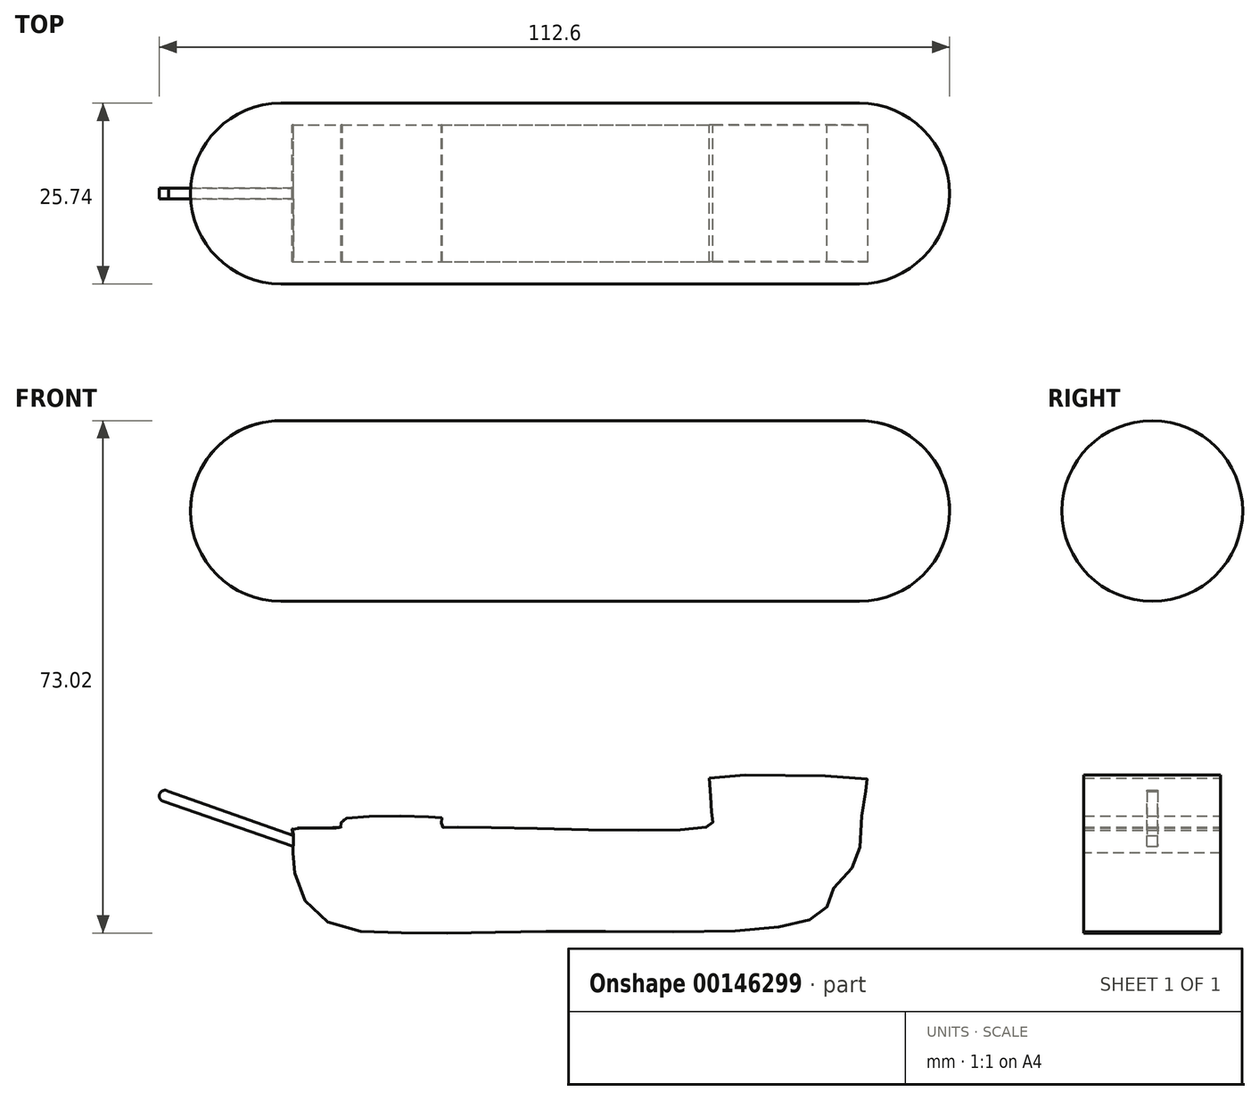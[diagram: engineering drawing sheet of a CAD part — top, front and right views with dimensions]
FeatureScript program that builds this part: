
annotation { "Feature Type Name" : "Feature", "Feature Type Description" : "" }
export const myFeature = defineFeature(function(context is Context, id is Id, definition is map)
    precondition{}
    {
        {
            var Q0;
            Q0=qCreatedBy(makeId("Front.planeOp"),FACE);
            var sketch = newSketch(context, id + "F0", { "sketchPlane" : qUnion([Q0])});
            skLineSegment(sketch, "E0.top", {"start": v(0, 25.75) * mm, "end": v(-41.2, 25.75) * mm});
            skLineSegment(sketch, "E0.left", {"start": v(0, 0) * mm, "end": v(0, 25.75) * mm});
            skLineSegment(sketch, "E0.right", {"start": v(-41.2, 12.87) * mm, "end": v(-41.2, 25.75) * mm});
            skArc(sketch, "E1", {"start": v(-41.2, 25.75) * mm, "mid": v(-50.3, 21.98) * mm, "end": v(-54.07, 12.87) * mm});
            skLineSegment(sketch, "E2.MirrorCS", {"start": v(0, 25.75) * mm, "end": v(41.2, 25.75) * mm});
            skLineSegment(sketch, "E3.MirrorCS", {"start": v(41.2, 12.87) * mm, "end": v(41.2, 25.75) * mm});
            skArc(sketch, "E4.MirrorCS", {"start": v(41.2, 25.75) * mm, "mid": v(50.3, 21.98) * mm, "end": v(54.07, 12.87) * mm});
            skPoint(sketch, "E5", {"position": v(-54.07, 12.87) * mm});
            skPoint(sketch, "E6", {"position": v(54.07, 12.87) * mm});
            skPoint(sketch, "E7", {"position": v(0, 12.87) * mm});
            skLineSegment(sketch, "E8", {"start": v(-54.07, 12.87) * mm, "end": v(54.07, 12.87) * mm});
            skPoint(sketch, "E0.bottom.end.orphan", {"position": v(-41.2, 0) * mm});
            skPoint(sketch, "E9.MirrorCS.end.orphan", {"position": v(41.2, 0) * mm});
            skPoint(sketch, "E9.MirrorCS.start.orphan", {"position": v(0, 0) * mm});
            skSolve(sketch);
        }
        {
            var Q0;
            Q0 = qSketchRegion(id + "F0", true);
            var Q1;
            Q1=sQuery(id+"F0.wireOp",EDGE,"E8");
            revolve(context, id + "F1", {"entities" : qUnion([Q0]), "axis" : qUnion([Q1]), "revolveType" : RevolveType.FULL});
        }
        {
            var Q0;
            Q0=qCreatedBy(makeId("Front.planeOp"),FACE);
            var sketch = newSketch(context, id + "F2", { "sketchPlane" : qUnion([Q0])});
            skFitSpline(sketch, "E10", {"points": [v(-39.5, -35.84) * mm, v(-39.36, -37.91) * mm, v(-37.93, -42.35) * mm, v(-33.64, -46.15) * mm, v(-25.83, -47.22) * mm, v(-13.51, -47.22) * mm, v(2.6, -47) * mm, v(25.73, -46.87) * mm, v(33.17, -45.65) * mm, v(36.47, -44.07) * mm, v(36.68, -42.14) * mm, v(39.12, -39.35) * mm, v(40.98, -36.34) * mm, v(41.48, -32.9) * mm, v(41.98, -27.17) * mm, v(42.34, -26.96) * mm, v(42.4, -25.6) * mm, v(41.77, -25.17) * mm, v(19.93, -25.03) * mm, v(19.85, -25.17) * mm], "startDerivative": vector(1.21, -55.72) * mm, "endDerivative": vector(5.24, -16.03) * mm});
            skFitSpline(sketch, "E11", {"points": [v(-39.5, -35.84) * mm, v(-39.5, -32.76) * mm, v(-39.5, -32.4) * mm, v(-32.56, -32.11) * mm, v(-32.56, -31.61) * mm, v(-32.28, -31.04) * mm, v(-18.38, -30.83) * mm, v(-18.24, -30.97) * mm, v(-18.31, -32.04) * mm, v(-17.3, -32.19) * mm, v(19.78, -32.11) * mm, v(20.28, -31.11) * mm, v(19.85, -25.17) * mm], "startDerivative": vector(3.23, 48.22) * mm, "endDerivative": vector(-3.51, 65.33) * mm});
            skLineSegment(sketch, "E12", {"start": v(-39.42, -34.57) * mm, "end": v(-57.4, -29.72) * mm});
            skLineSegment(sketch, "E13", {"start": v(-57.4, -29.72) * mm, "end": v(-57.13, -28.67) * mm});
            skLineSegment(sketch, "E14", {"start": v(-57.13, -28.67) * mm, "end": v(-39.42, -33.45) * mm});
            skSolve(sketch);
        }
        {
            var Q0;
            Q0=makeQuery(id+"F2.imprint","IMPRINT",FACE,{"disambiguationData":[TD([[makeQuery(id+"F2.imprint","IMPRINT",EDGE,{"derivedFrom":sQuery(id+"F2.wireOp",EDGE,"E10")}),1.0]])]});
            extrude(context, id + "F3", {"entities" : qUnion([Q0]), "endBound" : BoundingType.SYMMETRIC, "depth" : 19.5 * mm});
        }
        {
            var Q0;
            Q0=qCreatedBy(makeId("Front.planeOp"),FACE);
            var sketch = newSketch(context, id + "F4", { "sketchPlane" : qUnion([Q0])});
            skLineSegment(sketch, "E15", {"start": v(-39.42, -34.95) * mm, "end": v(-57.98, -28.5) * mm});
            skArc(sketch, "E16", {"start": v(-57.22, -27.1) * mm, "mid": v(-58.43, -27.36) * mm, "end": v(-57.98, -28.5) * mm});
            skLineSegment(sketch, "E17", {"start": v(-57.22, -27.1) * mm, "end": v(-39.23, -33.49) * mm});
            skLineSegment(sketch, "E18", {"start": v(-39.23, -33.49) * mm, "end": v(-39.42, -34.95) * mm});
            skSolve(sketch);
        }
        {
            var Q0;
            Q0=makeQuery(id+"F4.imprint","IMPRINT",FACE,{"disambiguationData":[TD([[makeQuery(id+"F4.imprint","IMPRINT",EDGE,{"derivedFrom":sQuery(id+"F4.wireOp",EDGE,"E15")}),-1.0]])]});
            extrude(context, id + "F5", {"entities" : qUnion([Q0]), "operationType" : NewBodyOperationType.ADD, "endBound" : BoundingType.SYMMETRIC, "depth" : 1.5 * mm});
        }
    });
